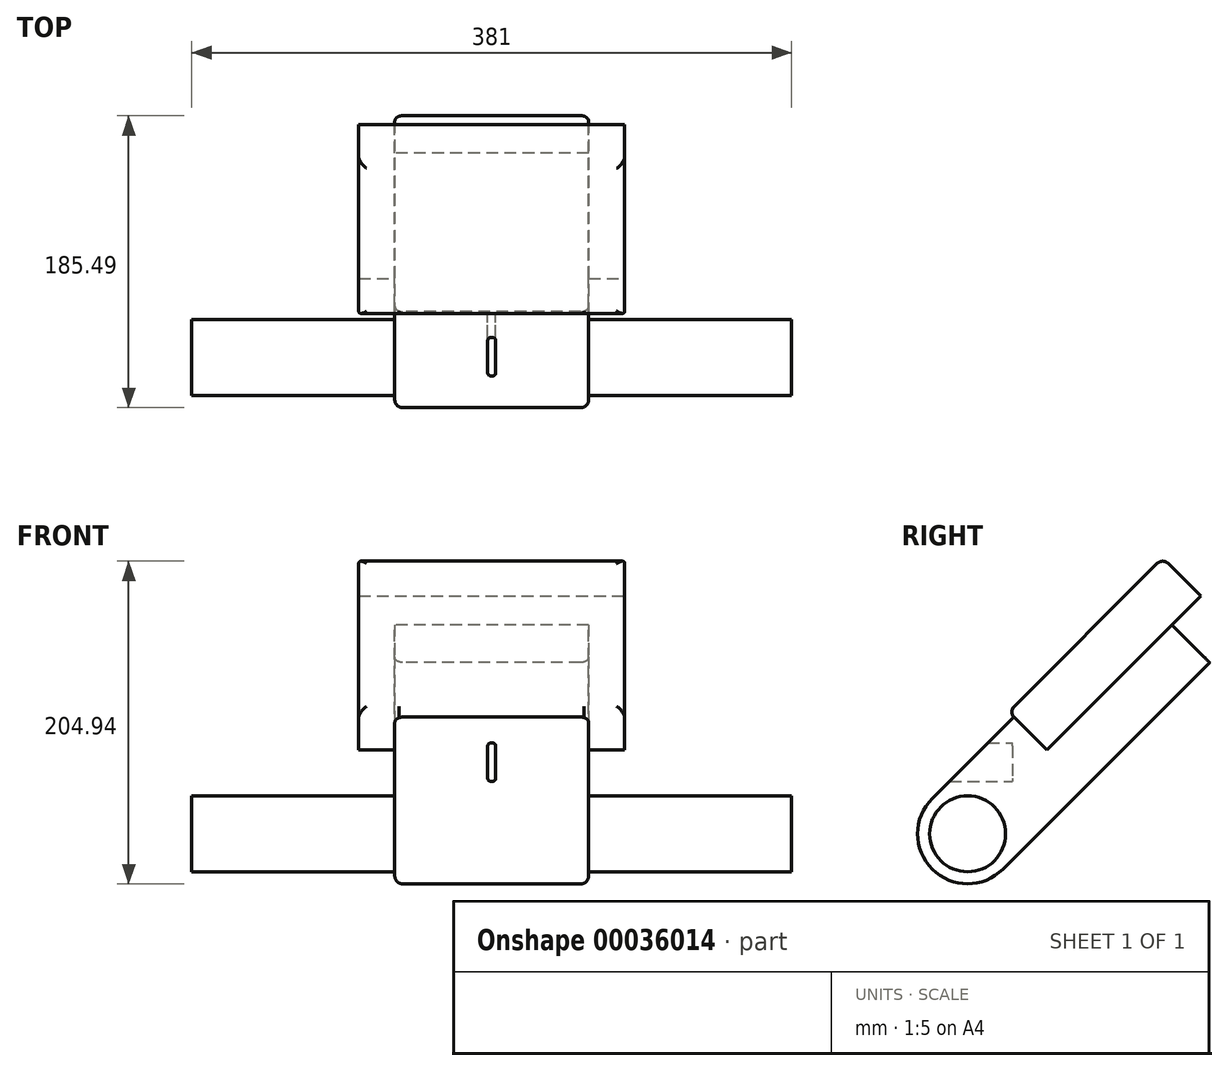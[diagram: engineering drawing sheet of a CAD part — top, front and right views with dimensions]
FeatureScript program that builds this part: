
annotation { "Feature Type Name" : "Feature", "Feature Type Description" : "" }
export const myFeature = defineFeature(function(context is Context, id is Id, definition is map)
    precondition{}
    {
        {
            var Q0;
            Q0=qCreatedBy(makeId("Top.planeOp"),FACE);
            var sketch = newSketch(context, id + "F0", { "sketchPlane" : qUnion([Q0])});
            skLineSegment(sketch, "E0", {"start": v(0, 0) * mm, "end": v(129.34, 0) * mm, "construction": true});
            skSolve(sketch);
        }
        {
            var Q0;
            Q0=sQuery(id+"F0.wireOp",EDGE,"E0");
            cPlane(context, id + "F1", {"entities" : qUnion([Q0]), "cplaneType" : CPlaneType.LINE_ANGLE, "offset" : 152.4 * mm, "angle" : 315 * degree, "width" : 152.4 * mm, "height" : 152.4 * mm});
        }
        {
            var Q0;
            Q0=qCreatedBy(makeId("Right.planeOp"),FACE);
            var sketch = newSketch(context, id + "F2", { "sketchPlane" : qUnion([Q0])});
            skArc(sketch, "E1", {"start": v(-22.45, 22.45) * mm, "mid": v(-22.45, -22.45) * mm, "end": v(22.45, -22.45) * mm});
            skLineSegment(sketch, "E2", {"start": v(-22.45, 22.45) * mm, "end": v(29.28, 74.18) * mm});
            skLineSegment(sketch, "E3", {"start": v(29.28, 74.18) * mm, "end": v(50.29, 53.16) * mm});
            skLineSegment(sketch, "E4", {"start": v(50.29, 53.16) * mm, "end": v(129.85, 132.73) * mm});
            skLineSegment(sketch, "E5", {"start": v(129.85, 132.73) * mm, "end": v(153.74, 108.84) * mm});
            skLineSegment(sketch, "E6", {"start": v(153.74, 108.84) * mm, "end": v(22.45, -22.45) * mm});
            skCircle(sketch, "E7", {"center": v(0, 0) * mm, "radius": 24.13 * mm, "construction": true});
            skLineSegment(sketch, "E8", {"start": v(123.93, 175.3) * mm, "end": v(0, 51.37) * mm, "construction": true});
            skLineSegment(sketch, "E9", {"start": v(123.93, 175.3) * mm, "end": v(142.85, 156.37) * mm, "construction": true});
            skSolve(sketch);
        }
        {
            var Q0;
            Q0 = qSketchRegion(id + "F2", true);
            extrude(context, id + "F3", {"entities" : qUnion([Q0]), "endBound" : BoundingType.SYMMETRIC, "depth" : 123.19 * mm});
        }
        {
            var Q0;
            Q0=makeQuery(id+"F3.opExtrude","SWEPT_FACE",FACE,{"disambiguationData":[OSD([sQuery(id+"F2.wireOp",EDGE,"E4")])]});
            var sketch = newSketch(context, id + "F4", { "sketchPlane" : qUnion([Q0])});
            skLineSegment(sketch, "E10.bottom", {"start": v(-84.45, 211.58) * mm, "end": v(84.45, 211.58) * mm});
            skLineSegment(sketch, "E10.top", {"start": v(-84.45, 73.15) * mm, "end": v(84.45, 73.15) * mm});
            skLineSegment(sketch, "E10.left", {"start": v(-84.46, 211.58) * mm, "end": v(-84.46, 73.15) * mm});
            skLineSegment(sketch, "E10.right", {"start": v(84.46, 211.58) * mm, "end": v(84.46, 73.15) * mm});
            skPoint(sketch, "E11", {"position": v(0, 73.15) * mm});
            skSolve(sketch);
        }
        {
            var Q0;
            Q0 = qSketchRegion(id + "F4", true);
            extrude(context, id + "F5", {"entities" : qUnion([Q0]), "operationType" : NewBodyOperationType.ADD, "depth" : 34.3 * mm});
        }
        {
            var Q0;
            Q0=qCreatedBy(makeId("Right.planeOp"),FACE);
            var sketch = newSketch(context, id + "F6", { "sketchPlane" : qUnion([Q0])});
            skLineSegment(sketch, "E12.bottom", {"start": v(-51.56, 57.65) * mm, "end": v(28.57, 57.65) * mm});
            skLineSegment(sketch, "E12.top", {"start": v(-51.56, 33.4) * mm, "end": v(28.57, 33.4) * mm});
            skLineSegment(sketch, "E12.left", {"start": v(-51.56, 57.65) * mm, "end": v(-51.56, 33.4) * mm});
            skLineSegment(sketch, "E12.right", {"start": v(28.57, 57.65) * mm, "end": v(28.57, 33.4) * mm});
            skPoint(sketch, "E13", {"position": v(12.75, 57.65) * mm});
            skPoint(sketch, "E14", {"position": v(-11.5, 33.4) * mm});
            skSolve(sketch);
        }
        {
            var Q0;
            Q0 = qSketchRegion(id + "F6", true);
            extrude(context, id + "F7", {"entities" : qUnion([Q0]), "operationType" : NewBodyOperationType.REMOVE, "endBound" : BoundingType.SYMMETRIC, "oppositeDirection" : true, "depth" : 5.08 * mm});
        }
        {
            var Q0;
            Q0=makeQuery(id+"F7.boolean.opBoolean","COPY",EDGE,{"derivedFrom":makeQuery(id+"F7.opExtrude","CAP_EDGE",EDGE,{"disambiguationData":[OSD([sQuery(id+"F6.wireOp",EDGE,"E12.bottom")])],"isStart":true})});
            var Q1;
            Q1=makeQuery(id+"F7.boolean.opBoolean","COPY",EDGE,{"derivedFrom":makeQuery(id+"F7.opExtrude","CAP_EDGE",EDGE,{"disambiguationData":[OSD([sQuery(id+"F6.wireOp",EDGE,"E12.bottom")])],"isStart":false})});
            var Q2;
            Q2=makeQuery(id+"F7.boolean.opBoolean","COPY",EDGE,{"derivedFrom":makeQuery(id+"F7.opExtrude","CAP_EDGE",EDGE,{"disambiguationData":[OSD([sQuery(id+"F6.wireOp",EDGE,"E12.top")])],"isStart":true})});
            var Q3;
            Q3=makeQuery(id+"F7.boolean.opBoolean","COPY",EDGE,{"derivedFrom":makeQuery(id+"F7.opExtrude","CAP_EDGE",EDGE,{"disambiguationData":[OSD([sQuery(id+"F6.wireOp",EDGE,"E12.top")])],"isStart":false})});
            fillet(context, id + "F8", {"entities" : qUnion([Q0, Q1, Q2, Q3]), "radius" : 1.78 * mm, "tangentPropagation" : true, "allowEdgeOverflow" : false});
        }
        {
            var Q0;
            Q0=makeQuery(id+"F3.opExtrude","CAP_EDGE",EDGE,{"disambiguationData":[OSD([sQuery(id+"F2.wireOp",EDGE,"E2")])],"isStart":true});
            var Q1;
            Q1=makeQuery(id+"F3.opExtrude","CAP_EDGE",EDGE,{"disambiguationData":[OSD([sQuery(id+"F2.wireOp",EDGE,"E2")])],"isStart":false});
            fillet(context, id + "F9", {"entities" : qUnion([Q0, Q1]), "radius" : 5.08 * mm, "tangentPropagation" : true, "allowEdgeOverflow" : false});
        }
        {
            var Q0;
            Q0=makeQuery(id+"F5.opExtrude","CAP_EDGE",EDGE,{"disambiguationData":[OSD([sQuery(id+"F4.wireOp",EDGE,"E10.right")])],"isStart":false});
            var Q1;
            Q1=makeQuery(id+"F5.opExtrude","CAP_EDGE",EDGE,{"disambiguationData":[OSD([sQuery(id+"F4.wireOp",EDGE,"E10.bottom")])],"isStart":false});
            var Q2;
            Q2=makeQuery(id+"F5.opExtrude","CAP_EDGE",EDGE,{"disambiguationData":[OSD([sQuery(id+"F4.wireOp",EDGE,"E10.left")])],"isStart":false});
            var Q3;
            Q3=makeQuery(id+"F5.opExtrude","CAP_EDGE",EDGE,{"disambiguationData":[OSD([sQuery(id+"F4.wireOp",EDGE,"E10.top")])],"isStart":false});
            fillet(context, id + "F10", {"entities" : qUnion([Q0, Q1, Q2, Q3]), "radius" : 5.08 * mm, "tangentPropagation" : true, "allowEdgeOverflow" : false});
        }
        {
            var Q0;
            Q0=qCreatedBy(makeId("Right.planeOp"),FACE);
            var sketch = newSketch(context, id + "F11", { "sketchPlane" : qUnion([Q0])});
            skCircle(sketch, "E15", {"center": v(0, 0) * mm, "radius": 24.13 * mm});
            skSolve(sketch);
        }
        {
            var Q0;
            Q0 = qSketchRegion(id + "F11", true);
            extrude(context, id + "F12", {"entities" : qUnion([Q0]), "operationType" : NewBodyOperationType.ADD, "endBound" : BoundingType.SYMMETRIC, "depth" : 381 * mm});
        }
    });
